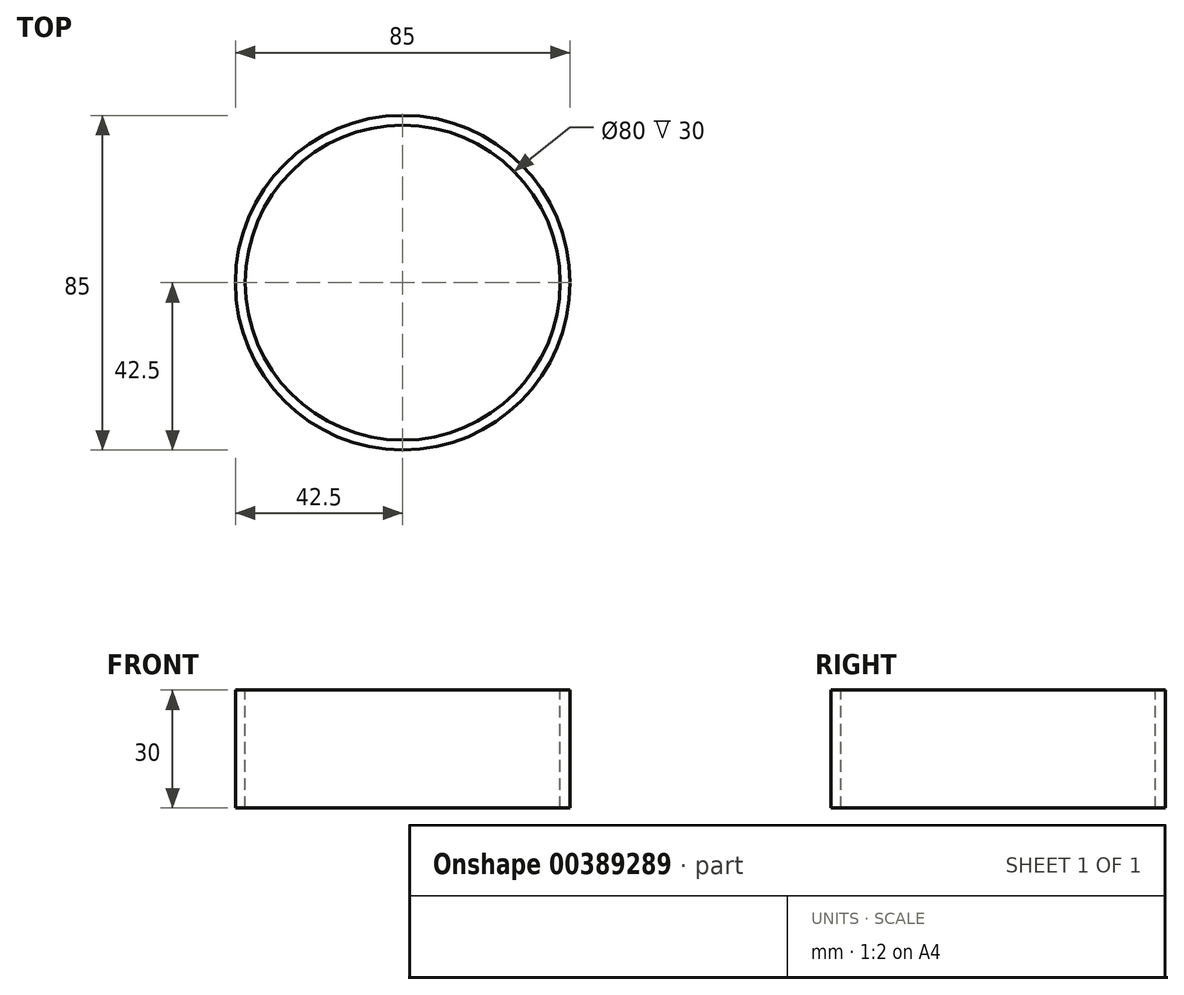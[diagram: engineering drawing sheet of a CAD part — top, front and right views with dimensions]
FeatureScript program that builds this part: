
annotation { "Feature Type Name" : "Feature", "Feature Type Description" : "" }
export const myFeature = defineFeature(function(context is Context, id is Id, definition is map)
    precondition{}
    {
        {
            var Q0;
            Q0=qCreatedBy(makeId("Front.planeOp"),FACE);
            var sketch = newSketch(context, id + "F0", { "sketchPlane" : qUnion([Q0])});
            skLineSegment(sketch, "E0.bottom", {"start": v(-66.73, 60) * mm, "end": v(-24.23, 60) * mm});
            skLineSegment(sketch, "E0.top", {"start": v(-66.73, 30) * mm, "end": v(-24.23, 30) * mm});
            skLineSegment(sketch, "E0.left", {"start": v(-66.73, 60) * mm, "end": v(-66.73, 30) * mm});
            skLineSegment(sketch, "E0.right", {"start": v(-24.23, 60) * mm, "end": v(-24.23, 30) * mm});
            skSolve(sketch);
        }
        {
            var Q0;
            Q0=makeQuery(id+"F0.imprint","IMPRINT",FACE,{"disambiguationData":[TD([[makeQuery(id+"F0.imprint","IMPRINT",EDGE,{"derivedFrom":sQuery(id+"F0.wireOp",EDGE,"E0.bottom")}),-1.0]])]});
            var Q1;
            Q1=qConstructionFilter(qBodyType(qCreatedBy(id+"F0",EDGE),BodyType.WIRE),ConstructionObject.NO);
            var Q2;
            Q2=sQuery(id+"F0.wireOp",EDGE,"E0.right");
            revolve(context, id + "F1", {"surfaceOperationType" : NewSurfaceOperationType.NEW, "entities" : qUnion([Q0]), "surfaceEntities" : qUnion([Q1]), "axis" : qUnion([Q2]), "revolveType" : RevolveType.FULL});
        }
        {
            var Q0;
            Q0=makeQuery(id+"F1.opRevolve","SWEPT_FACE",FACE,{"disambiguationData":[OSD([sQuery(id+"F0.wireOp",EDGE,"E0.bottom")])]});
            var Q1;
            Q1=makeQuery(id+"F1.opRevolve","SWEPT_FACE",FACE,{"disambiguationData":[OSD([sQuery(id+"F0.wireOp",EDGE,"E0.top")])]});
            shell(context, id + "F2", {"entities" : qUnion([Q0, Q1]), "thickness" : 2.5 * mm});
        }
    });
